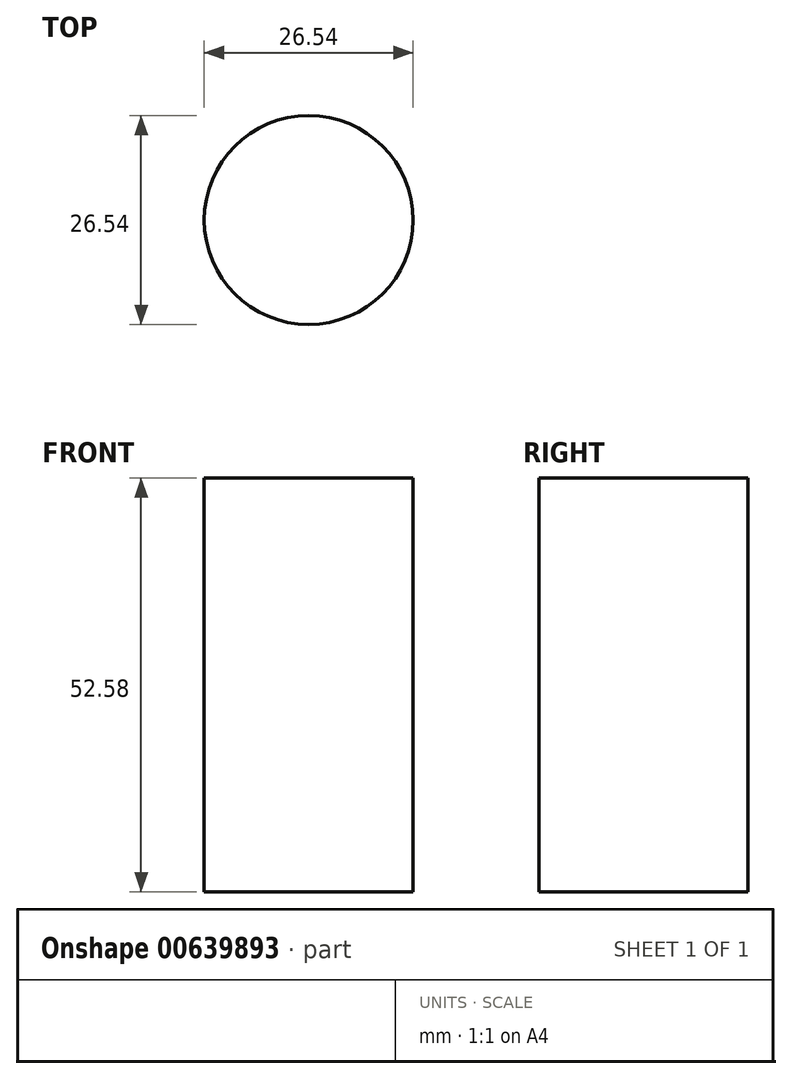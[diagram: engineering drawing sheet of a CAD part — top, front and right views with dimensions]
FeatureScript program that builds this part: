
annotation { "Feature Type Name" : "Feature", "Feature Type Description" : "" }
export const myFeature = defineFeature(function(context is Context, id is Id, definition is map)
    precondition{}
    {
        {
            var Q0;
            Q0=qCreatedBy(makeId("Top.planeOp"),FACE);
            var sketch = newSketch(context, id + "F0", { "sketchPlane" : qUnion([Q0])});
            skCircle(sketch, "E0", {"center": v(0, 0) * mm, "radius": 13.27 * mm});
            skSolve(sketch);
        }
        {
            var Q0;
            Q0 = qSketchRegion(id + "F0", true);
            extrude(context, id + "F1", {"entities" : qUnion([Q0]), "depth" : 52.58 * mm, "offsetDistance" : 25.4 * mm});
        }
    });
